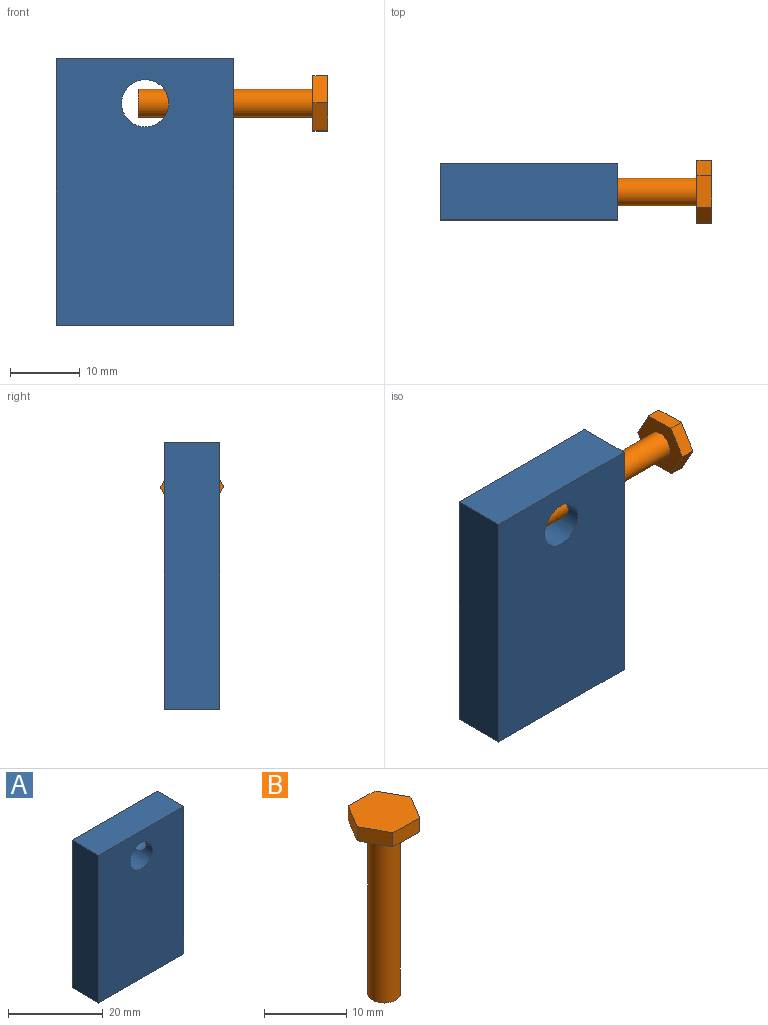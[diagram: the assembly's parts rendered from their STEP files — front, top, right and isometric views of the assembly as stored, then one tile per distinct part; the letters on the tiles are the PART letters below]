
ASSEMBLY  parts=2 mates=1
PART A: 8 faces, bbox 25.4x8x38.1 mm
  f0: cylinder r=3.38mm len=8mm, axis (0,-1,0), area 156.4mm2, adj f5,f6,f7
  f1: plane 38.1x8mm, normal (-1,0,0), area 304.8mm2, adj f2,f4,f5,f6
  f2: plane 25.4x8mm, normal (0,0,-1), area 203.2mm2, adj f1,f3,f5,f6
  f3: plane 38.1x8mm, normal (1,0,0), area 292.2mm2, adj f2,f4,f5,f6,f7
  f4: plane 25.4x8mm, normal (0,0,1), area 203.2mm2, adj f1,f3,f5,f6
  f5: plane 38.1x25.4mm, normal (0,-1,0), area 932mm2, adj f0,f1,f2,f3,f4
  f6: plane 38.1x25.4mm, normal (0,1,0), area 932mm2, adj f0,f1,f2,f3,f4
  f7: cylinder r=2mm len=9.98mm, axis (1,0,0), area 121.2mm2, adj f0,f3
PART B: 10 faces, bbox 9.1x7.9x27.1 mm
  f0: cylinder r=2mm len=25mm, axis (0,0,-1), area 314.2mm2, adj f1,f9
  f1: plane 4x4mm, normal (0,0,-1), area 12.6mm2, adj f0
  f2: plane 3.88x2.35mm, normal (-0.85,0.52,0), area 9.5mm2, adj f3,f7,f8,f9
  f3: plane 3.97x2.18mm, normal (-0.88,-0.48,0), area 9.5mm2, adj f2,f4,f8,f9
  f4: plane 4.53x2.1mm, normal (-0.02,-1,0), area 9.5mm2, adj f3,f5,f8,f9
  f5: plane 3.88x2.35mm, normal (0.85,-0.52,0), area 9.5mm2, adj f4,f6,f8,f9
  f6: plane 3.97x2.18mm, normal (0.88,0.48,0), area 9.5mm2, adj f5,f7,f8,f9
  f7: plane 4.53x2.1mm, normal (0.02,1,0), area 9.5mm2, adj f2,f6,f8,f9
  f8: plane 9.06x7.95mm, normal (0,0,1), area 53.4mm2, adj f2,f3,f4,f5,f6,f7
  f9: plane 9.06x7.95mm, normal (0,0,-1), area 40.8mm2, adj f0,f2,f3,f4,f5,f6,f7
PLACE A t=(-12.99,-1.75,2.63)mm
PLACE B rot(axis=(-0.58,0.58,-0.58),120deg) t=(-13.99,-5.75,15.33)mm
MATE parallel B.f0 <-> A.f7  axis (-1,0,0) through (-13.99,-5.75,15.33)mm
